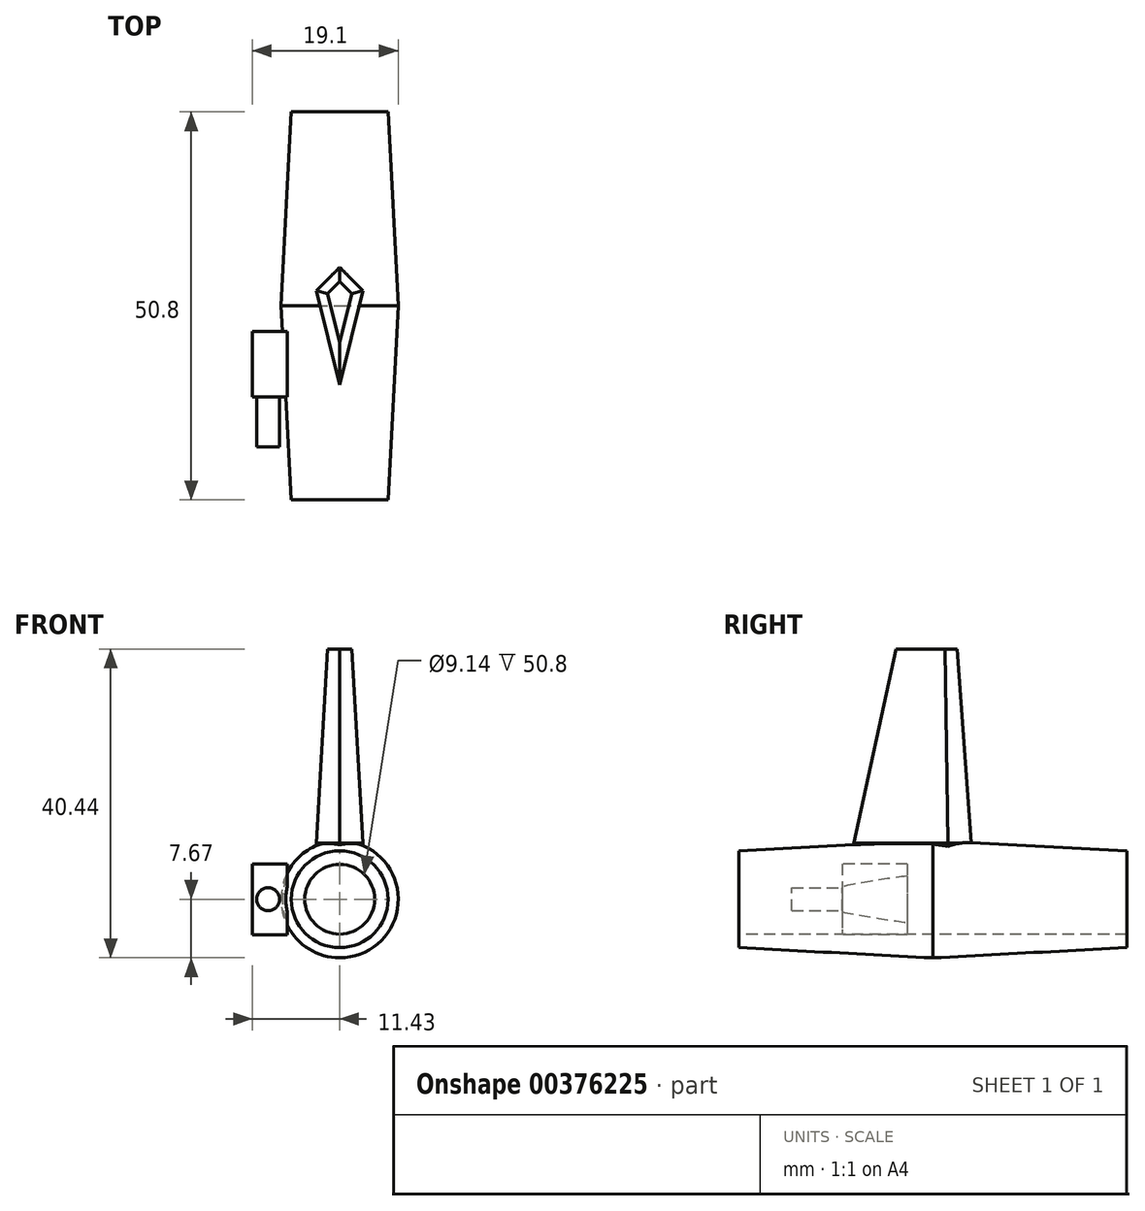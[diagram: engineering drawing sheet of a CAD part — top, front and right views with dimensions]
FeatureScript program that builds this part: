
annotation { "Feature Type Name" : "Feature", "Feature Type Description" : "" }
export const myFeature = defineFeature(function(context is Context, id is Id, definition is map)
    precondition{}
    {
        {
            var Q0;
            Q0=qCreatedBy(makeId("Front.planeOp"),FACE);
            var sketch = newSketch(context, id + "F0", { "sketchPlane" : qUnion([Q0])});
            skCircle(sketch, "E0", {"center": v(0, 0) * mm, "radius": 7.67 * mm});
            skSolve(sketch);
        }
        {
            var Q0;
            Q0=makeQuery(id+"F0.imprint","IMPRINT",FACE,{"disambiguationData":[TD([[makeQuery(id+"F0.imprint","IMPRINT",EDGE,{"derivedFrom":sQuery(id+"F0.wireOp",EDGE,"E0")}),1.0]])]});
            extrude(context, id + "F1", {"entities" : qUnion([Q0]), "depth" : 25.4 * mm, "hasDraft" : true, "draftAngle" : 3 * degree, "draftPullDirection" : true, "hasSecondDirection" : true, "secondDirectionOppositeDirection" : true, "secondDirectionDepth" : 25.4 * mm, "hasSecondDirectionDraft" : true, "secondDirectionDraftAngle" : 3 * degree, "secondDirectionDraftPullDirection" : true});
        }
        {
            var Q0;
            Q0=qCreatedBy(makeId("Top.planeOp"),FACE);
            cPlane(context, id + "F2", {"entities" : qUnion([Q0]), "cplaneType" : CPlaneType.OFFSET, "offset" : 7.37 * mm, "width" : 152.4 * mm, "height" : 152.4 * mm});
        }
        {
            var Q0;
            Q0=qCreatedBy(id+"F2.planeOp",FACE);
            var sketch = newSketch(context, id + "F3", { "sketchPlane" : qUnion([Q0])});
            skLineSegment(sketch, "E1", {"start": v(0, -10.34) * mm, "end": v(-3.06, 2) * mm});
            skLineSegment(sketch, "E2", {"start": v(-3.06, 2) * mm, "end": v(0, 5.06) * mm});
            skLineSegment(sketch, "E3", {"start": v(0, 5.06) * mm, "end": v(3.06, 2) * mm});
            skLineSegment(sketch, "E4", {"start": v(3.06, 2) * mm, "end": v(0, -10.34) * mm});
            skSolve(sketch);
        }
        {
            var Q0;
            Q0=makeQuery(id+"F3.imprint","IMPRINT",FACE,{"disambiguationData":[TD([[makeQuery(id+"F3.imprint","IMPRINT",EDGE,{"derivedFrom":sQuery(id+"F3.wireOp",EDGE,"E1")}),-1.0]])]});
            extrude(context, id + "F4", {"entities" : qUnion([Q0]), "operationType" : NewBodyOperationType.ADD, "depth" : 25.4 * mm, "hasDraft" : true, "draftAngle" : 3 * degree, "draftPullDirection" : true, "hasSecondDirection" : true, "secondDirectionOppositeDirection" : true, "secondDirectionDepth" : 13.72 * mm});
        }
        {
            var Q0;
            Q0=qCreatedBy(makeId("Right.planeOp"),FACE);
            cPlane(context, id + "F5", {"entities" : qUnion([Q0]), "cplaneType" : CPlaneType.OFFSET, "offset" : 6.86 * mm, "oppositeDirection" : true, "width" : 152.4 * mm, "height" : 152.4 * mm});
        }
        {
            var Q0;
            Q0=qCreatedBy(id+"F5.planeOp",FACE);
            var sketch = newSketch(context, id + "F6", { "sketchPlane" : qUnion([Q0])});
            skLineSegment(sketch, "E5.bottom", {"start": v(-3.33, 4.64) * mm, "end": v(-11.89, 4.64) * mm});
            skLineSegment(sketch, "E5.top", {"start": v(-3.33, -4.64) * mm, "end": v(-11.89, -4.64) * mm});
            skLineSegment(sketch, "E5.left", {"start": v(-3.33, 4.64) * mm, "end": v(-3.33, -4.64) * mm});
            skLineSegment(sketch, "E5.right", {"start": v(-11.89, 4.64) * mm, "end": v(-11.89, -4.64) * mm});
            skPoint(sketch, "E5.middle", {"position": v(-7.6, 0) * mm});
            skSolve(sketch);
        }
        {
            var Q0;
            Q0=makeQuery(id+"F6.imprint","IMPRINT",FACE,{"disambiguationData":[TD([[makeQuery(id+"F6.imprint","IMPRINT",EDGE,{"derivedFrom":sQuery(id+"F6.wireOp",EDGE,"E5.bottom")}),1.0]])]});
            extrude(context, id + "F7", {"entities" : qUnion([Q0]), "operationType" : NewBodyOperationType.ADD, "oppositeDirection" : true, "depth" : 4.57 * mm});
        }
        {
            var Q0;
            Q0=makeQuery(id+"F7.opExtrude","SWEPT_FACE",FACE,{"disambiguationData":[OSD([sQuery(id+"F6.wireOp",EDGE,"E5.right")])]});
            var sketch = newSketch(context, id + "F8", { "sketchPlane" : qUnion([Q0])});
            skCircle(sketch, "E6", {"center": v(-9.37, 0) * mm, "radius": 1.5 * mm});
            skSolve(sketch);
        }
        {
            var Q0;
            Q0=makeQuery(id+"F8.imprint","IMPRINT",FACE,{"disambiguationData":[TD([[makeQuery(id+"F8.imprint","IMPRINT",EDGE,{"derivedFrom":sQuery(id+"F8.wireOp",EDGE,"E6")}),1.0]])]});
            extrude(context, id + "F9", {"entities" : qUnion([Q0]), "operationType" : NewBodyOperationType.ADD, "depth" : 6.58 * mm});
        }
        {
            var Q0;
            Q0=makeQuery(id+"F1.opExtrude","CAP_FACE",FACE,{"disambiguationData":[OSD([sQuery(id+"F0.wireOp",EDGE,"E0")])],"isStart":false});
            var sketch = newSketch(context, id + "F10", { "sketchPlane" : qUnion([Q0])});
            skCircle(sketch, "E7", {"center": v(0, 0) * mm, "radius": 4.57 * mm});
            skSolve(sketch);
        }
        {
            var Q0;
            Q0=makeQuery(id+"F10.imprint","IMPRINT",FACE,{"disambiguationData":[TD([[makeQuery(id+"F10.imprint","IMPRINT",EDGE,{"derivedFrom":sQuery(id+"F10.wireOp",EDGE,"E7")}),1.0]])]});
            extrude(context, id + "F11", {"entities" : qUnion([Q0]), "operationType" : NewBodyOperationType.REMOVE, "oppositeDirection" : true, "depth" : 53.6 * mm});
        }
    });
